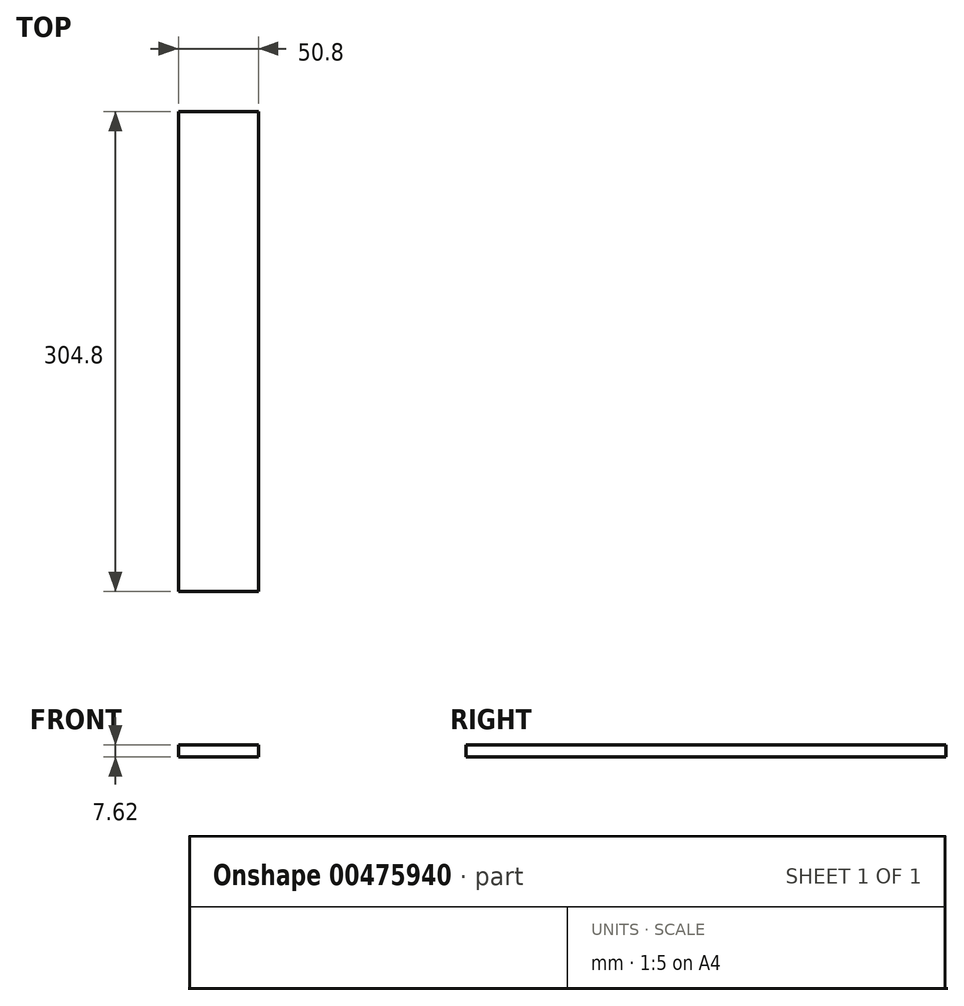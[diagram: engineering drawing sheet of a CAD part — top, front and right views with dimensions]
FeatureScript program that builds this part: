
annotation { "Feature Type Name" : "Feature", "Feature Type Description" : "" }
export const myFeature = defineFeature(function(context is Context, id is Id, definition is map)
    precondition{}
    {
        {
            var Q0;
            Q0=qCreatedBy(makeId("Top.planeOp"),FACE);
            var sketch = newSketch(context, id + "F0", { "sketchPlane" : qUnion([Q0])});
            skLineSegment(sketch, "E0.bottom", {"start": v(-23, 22.8) * mm, "end": v(-73.8, 22.8) * mm});
            skLineSegment(sketch, "E0.top", {"start": v(-23, 327.6) * mm, "end": v(-73.8, 327.6) * mm});
            skLineSegment(sketch, "E0.left", {"start": v(-23, 22.8) * mm, "end": v(-23, 327.6) * mm});
            skLineSegment(sketch, "E0.right", {"start": v(-73.8, 22.8) * mm, "end": v(-73.8, 327.6) * mm});
            skPoint(sketch, "E0.middle", {"position": v(-48.4, 175.2) * mm});
            skSolve(sketch);
        }
        {
            var Q0;
            Q0=makeQuery(id+"F0.imprint","IMPRINT",FACE,{"disambiguationData":[TD([[makeQuery(id+"F0.imprint","IMPRINT",EDGE,{"derivedFrom":sQuery(id+"F0.wireOp",EDGE,"E0.bottom")}),-1.0]])]});
            extrude(context, id + "F1", {"entities" : qUnion([Q0]), "depth" : 7.62 * mm});
        }
    });
